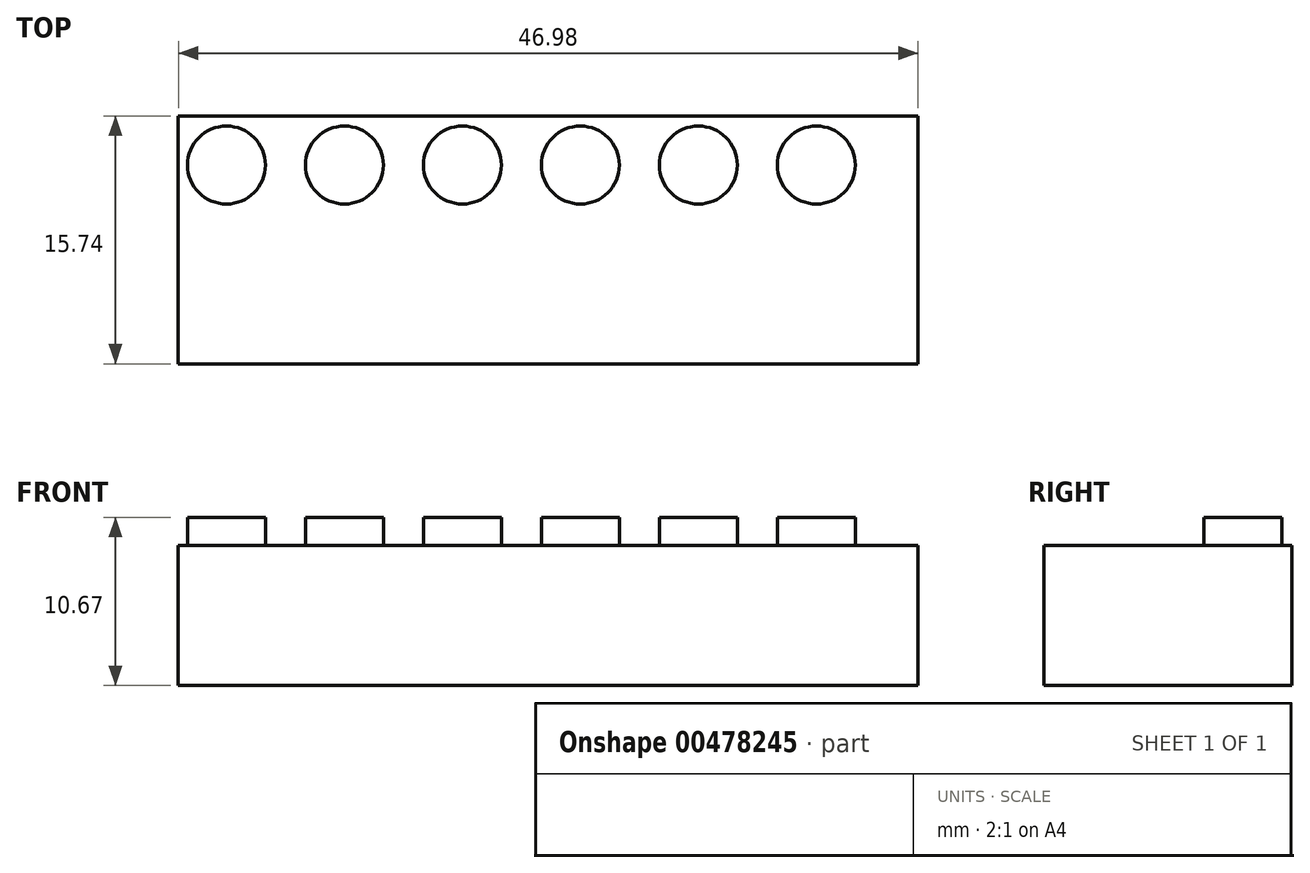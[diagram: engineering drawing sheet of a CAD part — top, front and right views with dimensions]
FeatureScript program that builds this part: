
annotation { "Feature Type Name" : "Feature", "Feature Type Description" : "" }
export const myFeature = defineFeature(function(context is Context, id is Id, definition is map)
    precondition{}
    {
        {
            var Q0;
            Q0=qCreatedBy(makeId("Top.planeOp"),FACE);
            var sketch = newSketch(context, id + "F0", { "sketchPlane" : qUnion([Q0])});
            skLineSegment(sketch, "E0.bottom", {"start": v(-23.5, 7.87) * mm, "end": v(23.5, 7.87) * mm});
            skLineSegment(sketch, "E0.top", {"start": v(-23.5, -7.87) * mm, "end": v(23.5, -7.87) * mm});
            skLineSegment(sketch, "E0.left", {"start": v(-23.5, 7.87) * mm, "end": v(-23.5, -7.87) * mm});
            skLineSegment(sketch, "E0.right", {"start": v(23.5, 7.87) * mm, "end": v(23.5, -7.87) * mm});
            skPoint(sketch, "E0.middle", {"position": v(0, 0) * mm});
            skSolve(sketch);
        }
        {
            var Q0;
            Q0=makeQuery(id+"F0.imprint","IMPRINT",FACE,{"disambiguationData":[TD([[makeQuery(id+"F0.imprint","IMPRINT",EDGE,{"derivedFrom":sQuery(id+"F0.wireOp",EDGE,"E0.bottom")}),-1.0]])]});
            extrude(context, id + "F1", {"entities" : qUnion([Q0]), "depth" : 8.9 * mm});
        }
        {
            var Q0;
            Q0=makeQuery(id+"F1.opExtrude","CAP_FACE",FACE,{"disambiguationData":[OSD([sQuery(id+"F0.wireOp",EDGE,"E0.bottom"),sQuery(id+"F0.wireOp",EDGE,"E0.top"),sQuery(id+"F0.wireOp",EDGE,"E0.left"),sQuery(id+"F0.wireOp",EDGE,"E0.right")])],"isStart":false});
            var sketch = newSketch(context, id + "F2", { "sketchPlane" : qUnion([Q0])});
            skCircle(sketch, "E1", {"center": v(-20.43, 4.76) * mm, "radius": 2.48 * mm});
            skSolve(sketch);
        }
        {
            var Q0;
            Q0 = qSketchRegion(id + "F2", true);
            extrude(context, id + "F3", {"entities" : qUnion([Q0]), "operationType" : NewBodyOperationType.ADD, "depth" : 1.78 * mm});
        }
        {
            var Q0;
            Q0=makeQuery(id+"F1.opExtrude","CAP_FACE",FACE,{"disambiguationData":[OSD([sQuery(id+"F0.wireOp",EDGE,"E0.bottom"),sQuery(id+"F0.wireOp",EDGE,"E0.top"),sQuery(id+"F0.wireOp",EDGE,"E0.left"),sQuery(id+"F0.wireOp",EDGE,"E0.right")])],"isStart":false});
            var sketch = newSketch(context, id + "F4", { "sketchPlane" : qUnion([Q0])});
            skCircle(sketch, "E2", {"center": v(-12.94, 4.76) * mm, "radius": 2.48 * mm});
            skCircle(sketch, "E3", {"center": v(-5.45, 4.76) * mm, "radius": 2.48 * mm});
            skCircle(sketch, "E4", {"center": v(2.04, 4.76) * mm, "radius": 2.48 * mm});
            skCircle(sketch, "E5", {"center": v(9.54, 4.76) * mm, "radius": 2.48 * mm});
            skCircle(sketch, "E6", {"center": v(17.03, 4.76) * mm, "radius": 2.48 * mm});
            skSolve(sketch);
        }
        {
            var Q0;
            Q0=sQuery(id+"F4.wireOp",EDGE,"E2");
            extrude(context, id + "F5", {"bodyType" : ToolBodyType.SURFACE, "surfaceEntities" : qUnion([Q0]), "depth" : 1.78 * mm});
        }
        {
            var Q0;
            Q0 = qSketchRegion(id + "F4", true);
            extrude(context, id + "F6", {"entities" : qUnion([Q0]), "operationType" : NewBodyOperationType.ADD, "depth" : 1.78 * mm});
        }
    });
